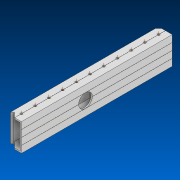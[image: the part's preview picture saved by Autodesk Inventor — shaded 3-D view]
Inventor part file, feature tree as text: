
AUTODESK INVENTOR PART (.ipt)
format: ipt  version: 2022.2 (Build 262287000, 287)  size: 536,576 bytes
history: native  units: in
note: dims shown in document units (in); Inventor stores cm internally (conversion verified against a paired STEP export)
features: other x16, extrude x4, sketch x4, pattern_linear x1, reference x1
ambient origin geometry x8: Origin, YZ Plane, XZ Plane, XY Plane, X Axis, Y Axis, Z Axis, Center Point
bodies: Solid1 (feature_tree)
feature tree (26):
  extrude  "Extrusion1"  Depth=2.0in
  other  "Work Axis1"
  pattern_linear  "Rectangular Pattern1"  Count1=11  [1 undecoded]
  extrude  "Extrusion2"  TaperAngle=0.0deg  [1 undecoded]
  extrude  "Extrusion3"  Depth=1.0in
  extrude  "Extrusion4"  TaperAngle=0.0deg  [1 undecoded]
  sketch  "Sketch1"  dims[d0=1.0in d1=2.0in]
  other  "Work Axis2"
  other  "Work Axis3"
  other  "Work Axis4"
  other  "Work Axis5"
  other  "Work Axis6"
  other  "Work Axis7"
  other  "Work Axis8"
  other  "Work Axis9"
  other  "Work Axis10"
  sketch  "Sketch2"  dims[d2=48.0in]
  sketch  "Sketch3"  dims[d3=0.0in d4=4.3307in]
  other  "Work Axis60"
  reference  "Reference3"
  sketch  "Sketch4"  dims[d6=1.0in d9=0.0in d10=0.0in d11=1.0in d12=0.0in d13=0.0in d15=0.3in d16=45.0deg d17=0.5in d18=0.1in d19=0.0in]
  other  "Cut-Extrude2"
  parser-record x1  (decoder bookkeeping rows leaked as tree rows — omitted from the tree; the rows remain in map.json)
  other  "Chassis.iam"
  other  "Plastic Clamping Bearing Block (217-4155):1"
  other  "217-4155-001 Rev6_2"
note: 3 required parameter values undecoded (feature->parameter linkage not recoverable at this tier; creation-order binding heuristic only, values carry confidence <= 0.55)
note: 1 file-system path scrubbed to <path> (originals preserved in map.json)
